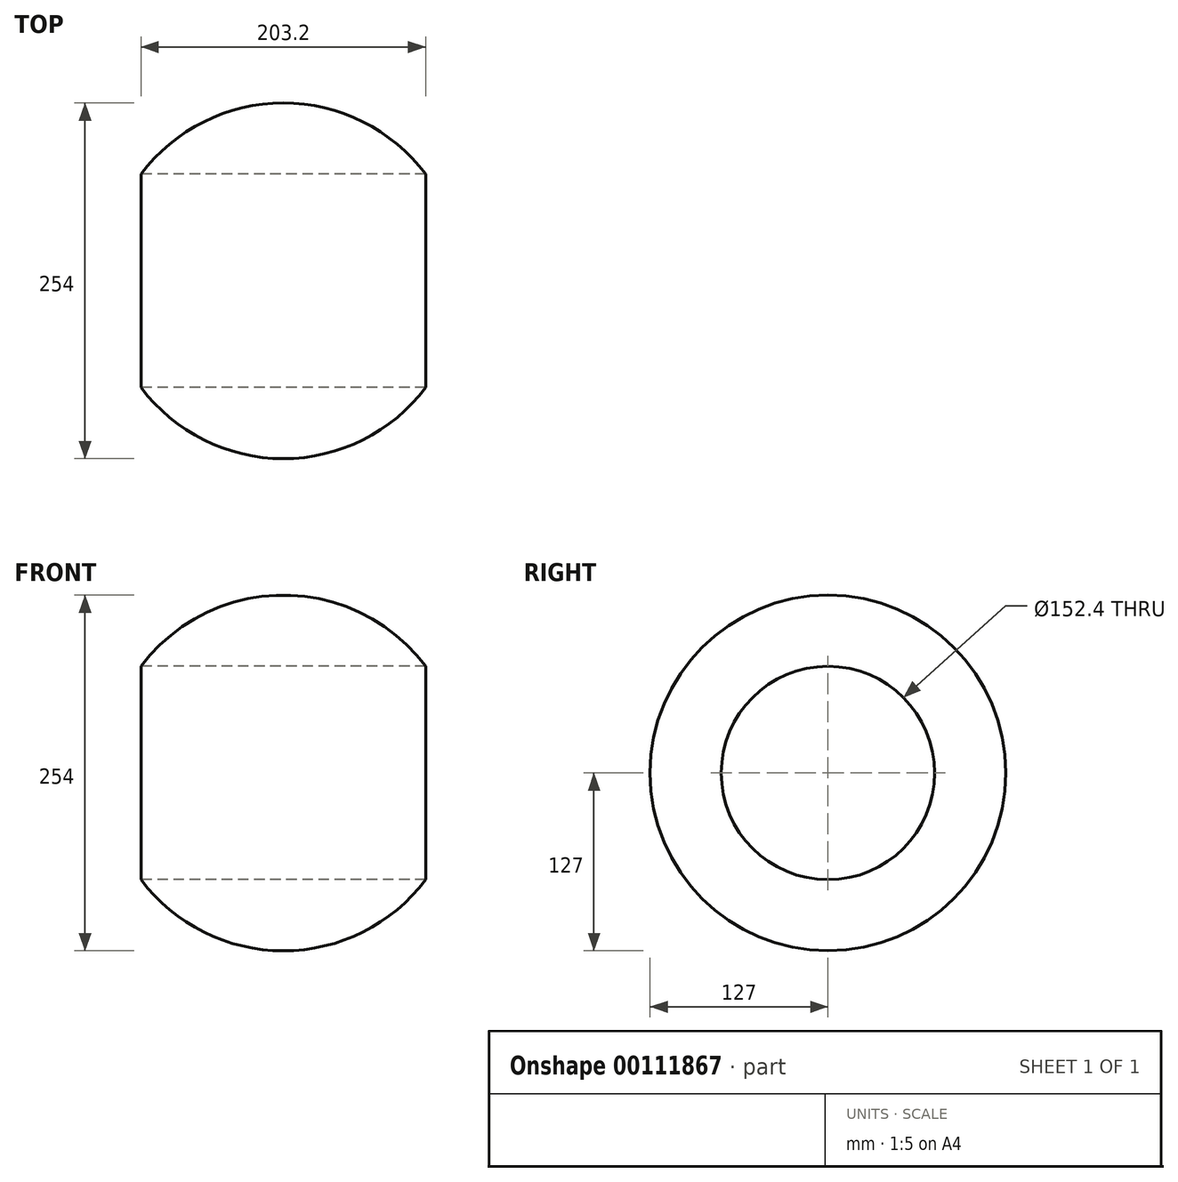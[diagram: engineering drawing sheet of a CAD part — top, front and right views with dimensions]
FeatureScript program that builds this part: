
annotation { "Feature Type Name" : "Feature", "Feature Type Description" : "" }
export const myFeature = defineFeature(function(context is Context, id is Id, definition is map)
    precondition{}
    {
        {
            var Q0;
            Q0=qCreatedBy(makeId("Front.planeOp"),FACE);
            var sketch = newSketch(context, id + "F0", { "sketchPlane" : qUnion([Q0])});
            skArc(sketch, "E0", {"start": v(127, 0) * mm, "mid": v(0, 127) * mm, "end": v(-127, 0) * mm});
            skLineSegment(sketch, "E1", {"start": v(-127, 0) * mm, "end": v(127, 0) * mm});
            skLineSegment(sketch, "E2", {"start": v(-101.6, 76.2) * mm, "end": v(101.6, 76.2) * mm});
            skSolve(sketch);
        }
        {
            var Q0;
            {var subQ0=sQuery(id+"F0.wireOp",EDGE,"E2");Q0=makeQuery(id+"F0.imprint","IMPRINT",FACE,{"disambiguationData":[TD([[makeQuery(id+"F0.imprint","IMPRINT",EDGE,{"derivedFrom":subQ0}),1.0]])]});}
            var Q1;
            Q1=sQuery(id+"F0.wireOp",EDGE,"E1");
            revolve(context, id + "F1", {"entities" : qUnion([Q0]), "axis" : qUnion([Q1]), "revolveType" : RevolveType.FULL});
        }
    });
